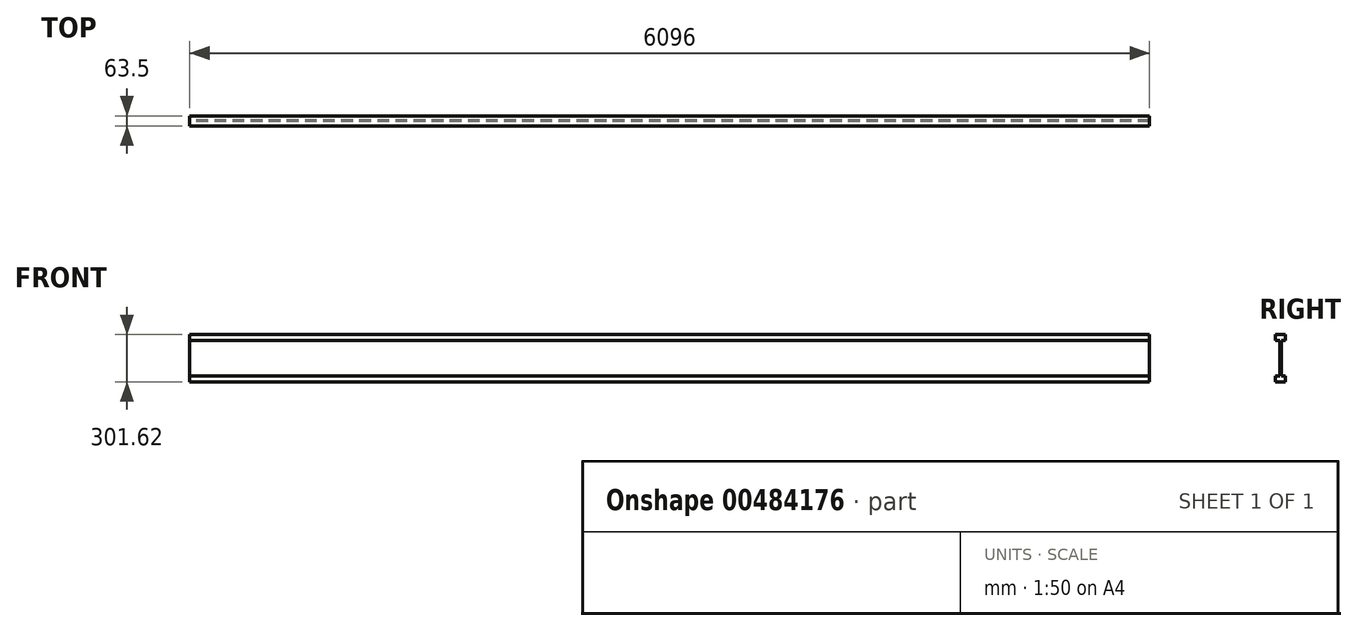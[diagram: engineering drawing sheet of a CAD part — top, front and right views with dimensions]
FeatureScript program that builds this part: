
annotation { "Feature Type Name" : "Feature", "Feature Type Description" : "" }
export const myFeature = defineFeature(function(context is Context, id is Id, definition is map)
    precondition{}
    {
        {
            var Q0;
            Q0=qCreatedBy(makeId("Right.planeOp"),FACE);
            var sketch = newSketch(context, id + "F0", { "sketchPlane" : qUnion([Q0])});
            skLineSegment(sketch, "E0", {"start": v(0, 0) * mm, "end": v(63.5, 0) * mm});
            skLineSegment(sketch, "E1", {"start": v(63.5, 0) * mm, "end": v(63.5, 38.1) * mm});
            skLineSegment(sketch, "E2", {"start": v(63.5, 38.1) * mm, "end": v(36.51, 38.1) * mm});
            skLineSegment(sketch, "E3", {"start": v(36.51, 38.1) * mm, "end": v(36.51, 263.53) * mm});
            skLineSegment(sketch, "E4", {"start": v(36.51, 263.53) * mm, "end": v(63.5, 263.53) * mm});
            skLineSegment(sketch, "E5", {"start": v(63.5, 263.53) * mm, "end": v(63.5, 301.63) * mm});
            skLineSegment(sketch, "E6", {"start": v(63.5, 301.63) * mm, "end": v(0, 301.63) * mm});
            skLineSegment(sketch, "E7", {"start": v(0, 301.63) * mm, "end": v(0, 263.53) * mm});
            skLineSegment(sketch, "E8", {"start": v(0, 263.53) * mm, "end": v(26.99, 263.53) * mm});
            skLineSegment(sketch, "E9", {"start": v(26.99, 263.53) * mm, "end": v(26.99, 38.1) * mm});
            skLineSegment(sketch, "E10", {"start": v(26.99, 38.1) * mm, "end": v(0, 38.1) * mm});
            skLineSegment(sketch, "E11", {"start": v(0, 38.1) * mm, "end": v(0, 0) * mm});
            skSolve(sketch);
        }
        {
            var Q0;
            Q0 = qSketchRegion(id + "F0", true);
            extrude(context, id + "F1", {"entities" : qUnion([Q0]), "depth" : 6096 * mm});
        }
    });
